# Revit family: P191568KX-130c_KFGC506J
name_source: partatom
category: Specialty Equipment
units: mm (PartAtom-declared; Revit-internal decimal feet)

## family parameters
Always vertical = Yes
Cut with Voids When Loaded = No
Enable Cutting in Views = No
Maintain Annotation Orientation = No
Part Type = Normal
Room Calculation Point = No
Round Connector Dimension = Use Diameter
Shared = No
Work Plane-Based = No

## types (1)
- KFGC506JSS
    Amps = 0 A
    Body Material = ARCAT - Metal - Steel - Stainless
    Clearance Material = ARCAT - Clearance
    Connector Material = ARCAT - Metal - Cast Iron
    Cooking Grate Material = ARCAT - Metal - Cast Iron 1/4" Plate
    Default Elevation = 0"
    Depth = 30 1/4"
    Description = KitchenAid® 36'' Smart Commercial-Style Gas Range with 6 Burners
KitchenAid® 36'' Smart Commercial-Style Gas Range with 6 Burners
    Dimension Guide = https://www.whirlpool.com
https://www.whirlpool.com
    Door Material = ARCAT - Metal - Steel - Stainless
    Family Name = COOKING
    Feature 1 = Even-Heat™ True Convection
Even-Heat™ True Convection
    Feature 2 = Two 20,000 BTU Ultra Power™ Dual-Flame Burners
Two 20,000 BTU Ultra Power™ Dual-Flame Burners
    Feature 3 = 5,000 BTU Simmer & Melt Burner
5,000 BTU Simmer & Melt Burner
    Glass Material = ARCAT - Glass - Tempered - Black
    Handle Material = ARCAT - Metal - Steel - Gray
    Height = 36"
    Installation-Fabrication = https://www.whirlpool.com
https://www.whirlpool.com
    Knob Material = ARCAT - Metal - Steel - Gray
    Leg Material = ARCAT - Plastic - Black
    Manufacturer = KitchenAid
    Model = KFGC506JSS
    Voltage = 0 V
    Width = 35 7/8"

## geometry (parser evidence)
native form markers: Sweep x6
no freeform markers — native parametric forms only
